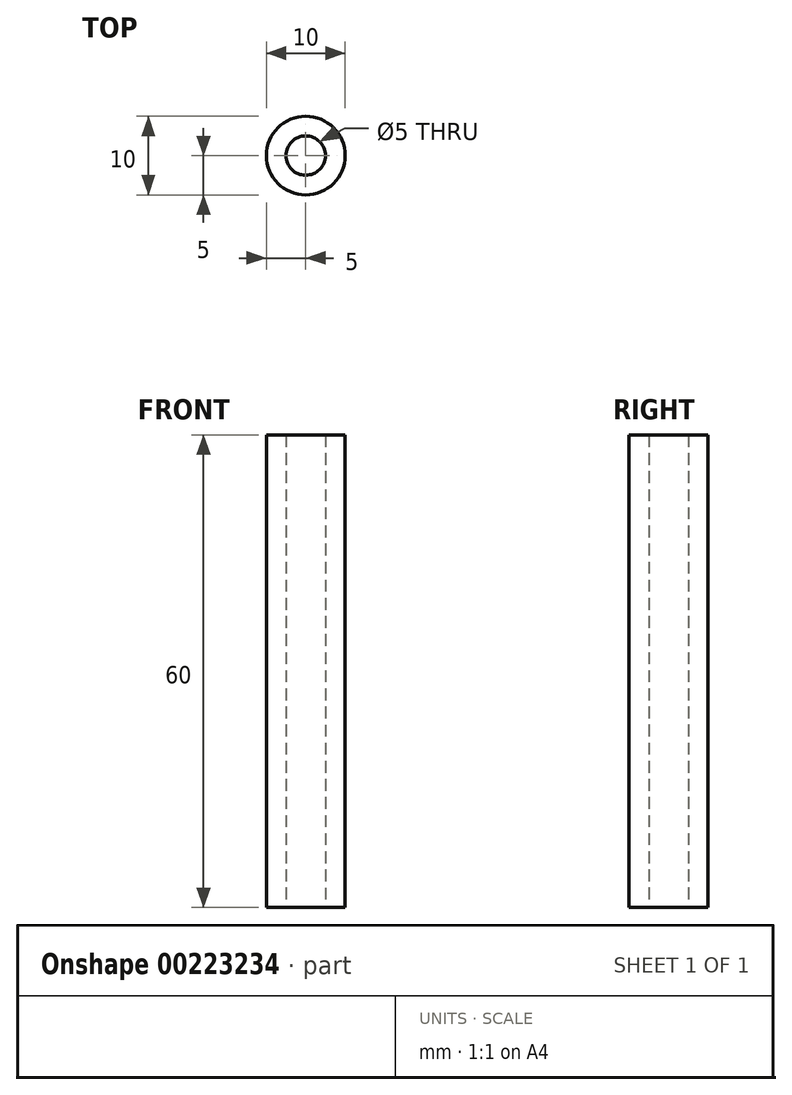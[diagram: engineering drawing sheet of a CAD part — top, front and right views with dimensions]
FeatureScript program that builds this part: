
annotation { "Feature Type Name" : "Feature", "Feature Type Description" : "" }
export const myFeature = defineFeature(function(context is Context, id is Id, definition is map)
    precondition{}
    {
        {
            var Q0;
            Q0=qCreatedBy(makeId("Top.planeOp"),FACE);
            var sketch = newSketch(context, id + "F0", { "sketchPlane" : qUnion([Q0])});
            skCircle(sketch, "E0", {"center": v(0, 0) * mm, "radius": 5 * mm});
            skCircle(sketch, "E1", {"center": v(0, 0) * mm, "radius": 2.5 * mm});
            skSolve(sketch);
        }
        {
            var Q0;
            Q0 = qSketchRegion(id + "F0", true);
            extrude(context, id + "F1", {"entities" : qUnion([Q0]), "depth" : 60 * mm});
        }
    });
